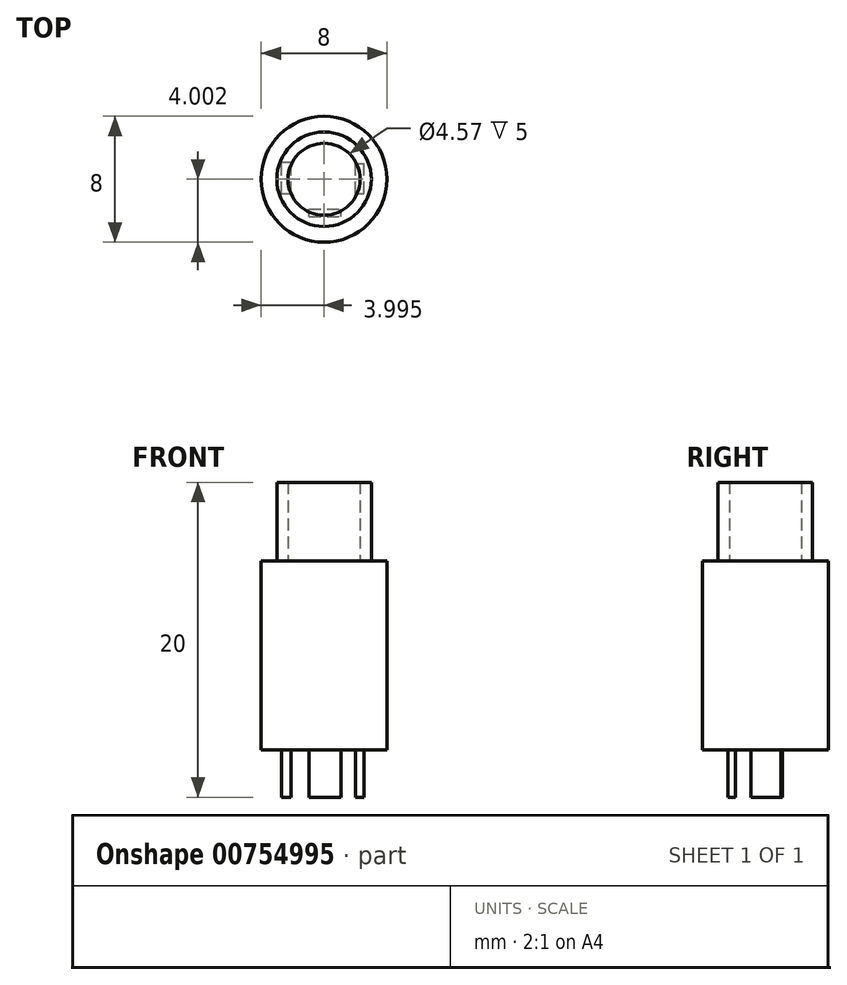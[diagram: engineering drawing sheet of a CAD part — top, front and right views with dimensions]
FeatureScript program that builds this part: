
annotation { "Feature Type Name" : "Feature", "Feature Type Description" : "" }
export const myFeature = defineFeature(function(context is Context, id is Id, definition is map)
    precondition{}
    {
        {
            var Q0;
            Q0=qCreatedBy(makeId("Top.planeOp"),FACE);
            var sketch = newSketch(context, id + "F0", { "sketchPlane" : qUnion([Q0])});
            skCircle(sketch, "E0", {"center": v(2.7, 0.9) * mm, "radius": 4 * mm});
            skSolve(sketch);
        }
        {
            var Q0;
            Q0 = qSketchRegion(id + "F0", true);
            extrude(context, id + "F1", {"entities" : qUnion([Q0]), "depth" : 12 * mm, "offsetDistance" : 25 * mm});
        }
        {
            var Q0;
            Q0=makeQuery(id+"F1.opExtrude","CAP_FACE",FACE,{"disambiguationData":[OSD([sQuery(id+"F0.wireOp",EDGE,"E0")])],"isStart":false});
            var sketch = newSketch(context, id + "F2", { "sketchPlane" : qUnion([Q0])});
            skCircle(sketch, "E1", {"center": v(2.7, 0.9) * mm, "radius": 3 * mm});
            skCircle(sketch, "E2", {"center": v(2.7, 0.9) * mm, "radius": 2.29 * mm});
            skSolve(sketch);
        }
        {
            var Q0;
            Q0 = qSketchRegion(id + "F2", true);
            extrude(context, id + "F3", {"entities" : qUnion([Q0]), "operationType" : NewBodyOperationType.ADD, "depth" : 5 * mm, "offsetDistance" : 25 * mm});
        }
        {
            var Q0;
            Q0=makeQuery(id+"F1.opExtrude","CAP_FACE",FACE,{"disambiguationData":[OSD([sQuery(id+"F0.wireOp",EDGE,"E0")])],"isStart":true});
            var sketch = newSketch(context, id + "F4", { "sketchPlane" : qUnion([Q0])});
            skLineSegment(sketch, "E3.bottom", {"start": v(0, 0) * mm, "end": v(0.61, 0) * mm});
            skLineSegment(sketch, "E3.top", {"start": v(0, -2) * mm, "end": v(0.61, -2) * mm});
            skLineSegment(sketch, "E3.left", {"start": v(0, 0) * mm, "end": v(0, -2) * mm});
            skLineSegment(sketch, "E3.right", {"start": v(0.61, 0) * mm, "end": v(0.61, -2) * mm});
            skLineSegment(sketch, "E4.bottom", {"start": v(4.7, 0) * mm, "end": v(5.24, 0) * mm});
            skLineSegment(sketch, "E4.top", {"start": v(4.7, -1.9) * mm, "end": v(5.24, -1.9) * mm});
            skLineSegment(sketch, "E4.left", {"start": v(4.7, 0) * mm, "end": v(4.7, -1.9) * mm});
            skLineSegment(sketch, "E4.right", {"start": v(5.24, 0) * mm, "end": v(5.24, -1.9) * mm});
            skLineSegment(sketch, "E5.bottom", {"start": v(1.76, 1.48) * mm, "end": v(3.77, 1.48) * mm});
            skLineSegment(sketch, "E5.top", {"start": v(1.76, 0.98) * mm, "end": v(3.77, 0.98) * mm});
            skLineSegment(sketch, "E5.left", {"start": v(1.76, 1.48) * mm, "end": v(1.76, 0.98) * mm});
            skLineSegment(sketch, "E5.right", {"start": v(3.77, 1.48) * mm, "end": v(3.77, 0.98) * mm});
            skSolve(sketch);
        }
        {
            var Q0;
            Q0 = qSketchRegion(id + "F4", true);
            extrude(context, id + "F5", {"entities" : qUnion([Q0]), "operationType" : NewBodyOperationType.ADD, "depth" : 3 * mm, "offsetDistance" : 25 * mm});
        }
    });
